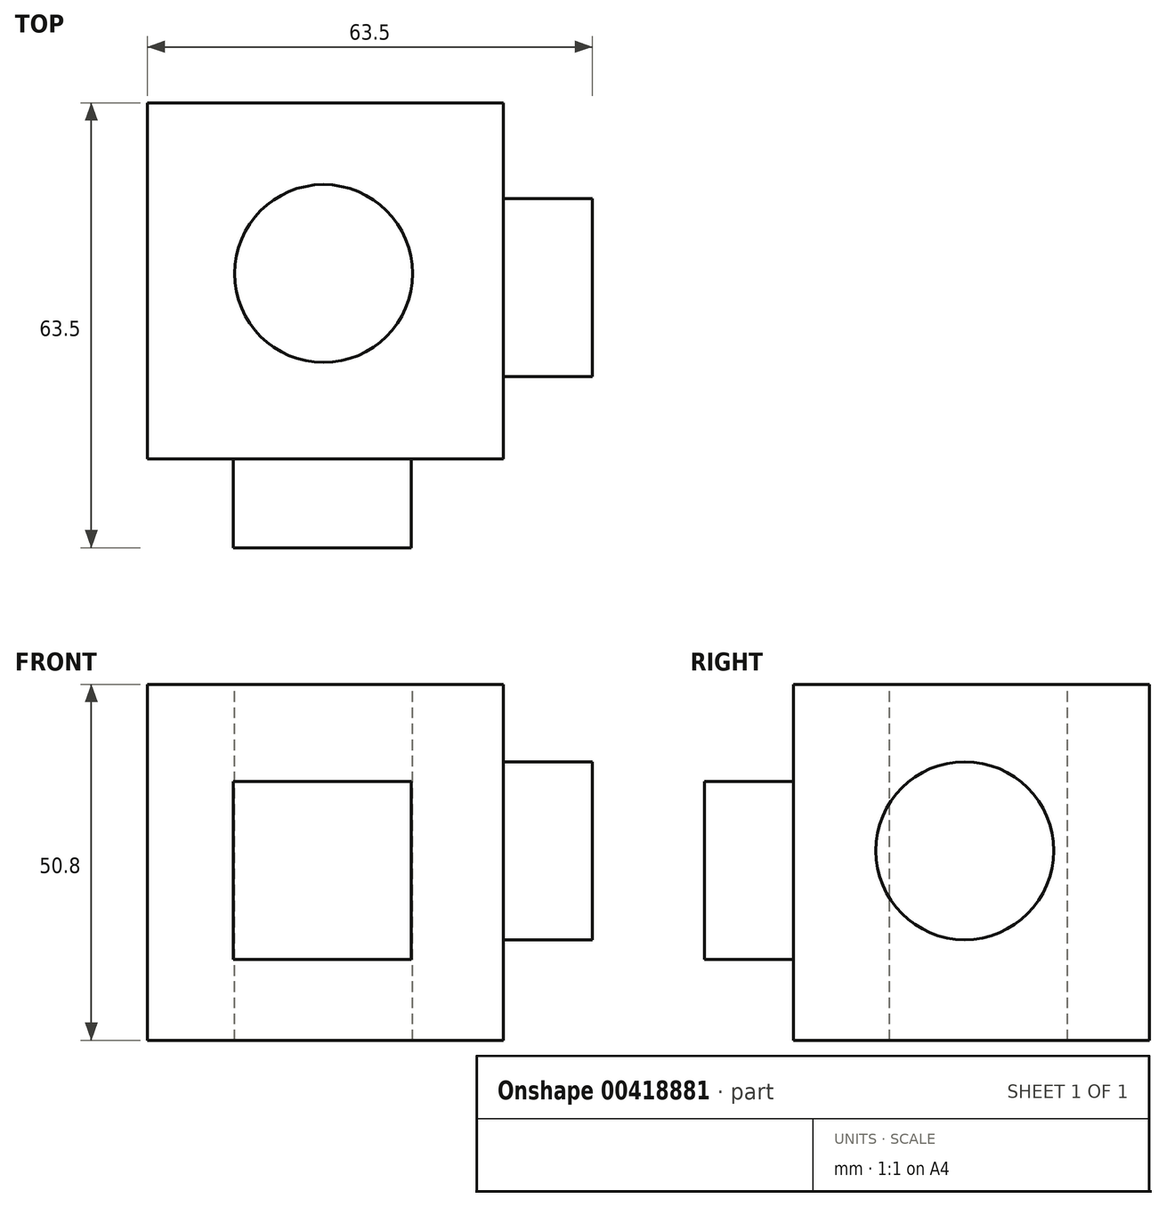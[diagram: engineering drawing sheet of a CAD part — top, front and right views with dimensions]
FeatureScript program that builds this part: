
annotation { "Feature Type Name" : "Feature", "Feature Type Description" : "" }
export const myFeature = defineFeature(function(context is Context, id is Id, definition is map)
    precondition{}
    {
        {
            var Q0;
            Q0=qCreatedBy(makeId("Front.planeOp"),FACE);
            var sketch = newSketch(context, id + "F0", { "sketchPlane" : qUnion([Q0])});
            skLineSegment(sketch, "E0", {"start": v(0, 0) * mm, "end": v(-62.25, 0) * mm});
            skLineSegment(sketch, "E1.bottom", {"start": v(0, 0) * mm, "end": v(-50.8, 0) * mm});
            skLineSegment(sketch, "E1.top", {"start": v(0, 50.8) * mm, "end": v(-50.8, 50.8) * mm});
            skLineSegment(sketch, "E1.left", {"start": v(0, 0) * mm, "end": v(0, 50.8) * mm});
            skLineSegment(sketch, "E1.right", {"start": v(-50.8, 0) * mm, "end": v(-50.8, 50.8) * mm});
            skSolve(sketch);
        }
        {
            var Q0;
            Q0 = qSketchRegion(id + "F0", true);
            extrude(context, id + "F1", {"entities" : qUnion([Q0]), "depth" : 50.8 * mm});
        }
        {
            var Q0;
            Q0=makeQuery(id+"F1.opExtrude","CAP_FACE",FACE,{"disambiguationData":[OSD([sQuery(id+"F0.wireOp",EDGE,"E1.bottom"),sQuery(id+"F0.wireOp",EDGE,"E1.top"),sQuery(id+"F0.wireOp",EDGE,"E1.left"),sQuery(id+"F0.wireOp",EDGE,"E1.right")])],"isStart":false});
            var sketch = newSketch(context, id + "F2", { "sketchPlane" : qUnion([Q0])});
            skLineSegment(sketch, "E2.bottom", {"start": v(-13.15, 11.53) * mm, "end": v(-38.55, 11.53) * mm});
            skLineSegment(sketch, "E2.top", {"start": v(-13.15, 36.93) * mm, "end": v(-38.55, 36.93) * mm});
            skLineSegment(sketch, "E2.left", {"start": v(-13.15, 11.53) * mm, "end": v(-13.15, 36.93) * mm});
            skLineSegment(sketch, "E2.right", {"start": v(-38.55, 11.53) * mm, "end": v(-38.55, 36.93) * mm});
            skSolve(sketch);
        }
        {
            var Q0;
            Q0 = qSketchRegion(id + "F2", true);
            extrude(context, id + "F3", {"entities" : qUnion([Q0]), "operationType" : NewBodyOperationType.ADD, "depth" : 12.7 * mm});
        }
        {
            var Q0;
            Q0=makeQuery(id+"F1.opExtrude","SWEPT_FACE",FACE,{"disambiguationData":[OSD([sQuery(id+"F0.wireOp",EDGE,"E1.left")])]});
            var sketch = newSketch(context, id + "F4", { "sketchPlane" : qUnion([Q0])});
            skCircle(sketch, "E3", {"center": v(-26.36, 27.05) * mm, "radius": 12.7 * mm});
            skSolve(sketch);
        }
        {
            var Q0;
            Q0 = qSketchRegion(id + "F4", true);
            extrude(context, id + "F5", {"entities" : qUnion([Q0]), "operationType" : NewBodyOperationType.ADD, "depth" : 12.7 * mm});
        }
        {
            var Q0;
            Q0=makeQuery(id+"F1.opExtrude","SWEPT_FACE",FACE,{"disambiguationData":[OSD([sQuery(id+"F0.wireOp",EDGE,"E1.top")])]});
            var sketch = newSketch(context, id + "F6", { "sketchPlane" : qUnion([Q0])});
            skCircle(sketch, "E4", {"center": v(-25.66, -24.38) * mm, "radius": 12.7 * mm});
            skSolve(sketch);
        }
        {
            var Q0;
            Q0 = qSketchRegion(id + "F6", true);
            extrude(context, id + "F7", {"entities" : qUnion([Q0]), "operationType" : NewBodyOperationType.REMOVE, "oppositeDirection" : true, "depth" : 50.8 * mm});
        }
    });
